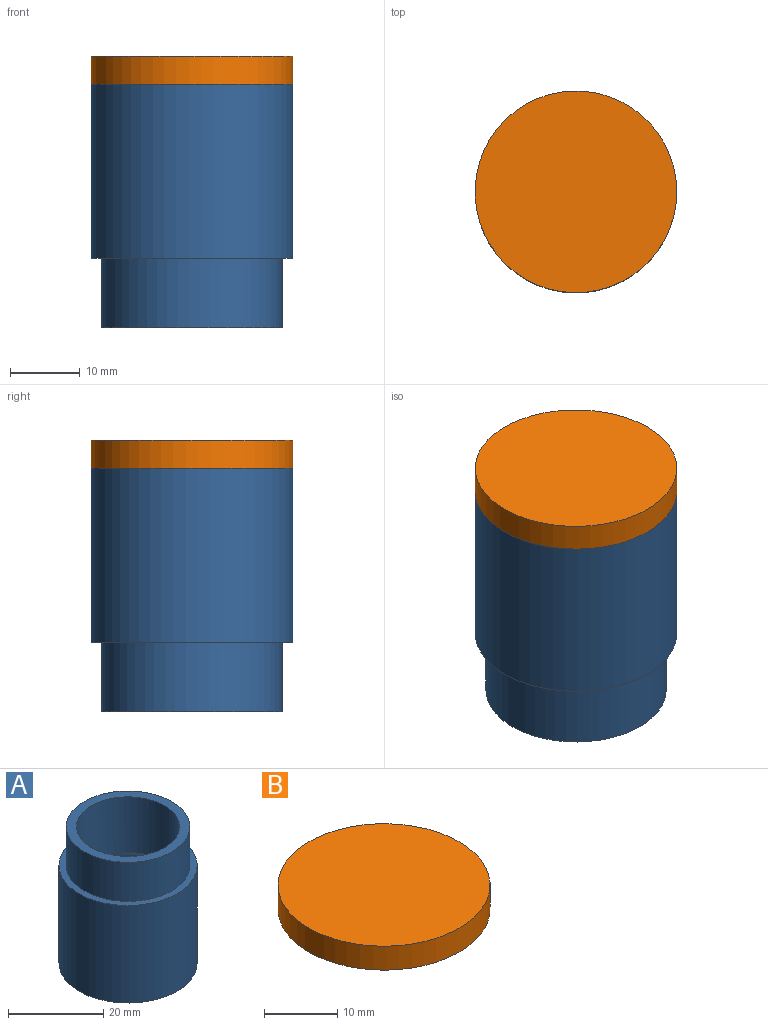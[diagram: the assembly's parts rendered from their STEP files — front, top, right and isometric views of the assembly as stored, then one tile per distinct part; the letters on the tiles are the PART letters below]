
ASSEMBLY  parts=2 mates=1
PART A: 10 faces, bbox 29x29x35 mm
  f0: cylinder r=14.48mm len=28.96mm, axis (0,0,-1), area 2274.5mm2, adj f1,f2
  f1: plane 28.96x28.96mm, normal (0,0,1), area 131.8mm2, adj f0,f5
  f2: plane 28.96x28.96mm, normal (0,0,-1), area 404.2mm2, adj f0,f4
  f3: cylinder r=12.5mm len=25mm, axis (0,0,1), area 863.9mm2, adj f8,f9
  f4: cylinder r=9mm len=18mm, axis (0,0,-1), area 254.5mm2, adj f2,f9
  f5: cylinder r=12.95mm len=25.9mm, axis (0,0,-1), area 813.7mm2, adj f1,f6
  f6: plane 25.9x25.9mm, normal (0,0,1), area 160.4mm2, adj f5,f7
  f7: cylinder r=10.8mm len=21.6mm, axis (0,0,1), area 970.4mm2, adj f6,f8
  f8: cone r=12.5mm half-angle=45deg, axis (0,0,-1), area 176mm2, adj f3,f7
  f9: cone r=7.5mm half-angle=45deg, axis (0,0,1), area 334.3mm2, adj f3,f4
PART B: 3 faces, bbox 29x29x4 mm
  f0: cylinder r=14.48mm len=28.96mm, axis (0,0,-1), area 363.9mm2, adj f1,f2
  f1: plane 28.96x28.96mm, normal (0,0,1), area 658.7mm2, adj f0
  f2: plane 28.96x28.96mm, normal (0,0,-1), area 658.7mm2, adj f0
PLACE A rot(axis=(-1,0,0),180deg) t=(-4.81,13.91,7.5)mm
PLACE B rot(axis=(0.34,-0.94,0.08),0deg) t=(-4.81,13.91,7.5)mm
MATE fastened A.f0 <-> B.f0  axis (0,0,1) through (-4.81,13.91,7.5)mm
